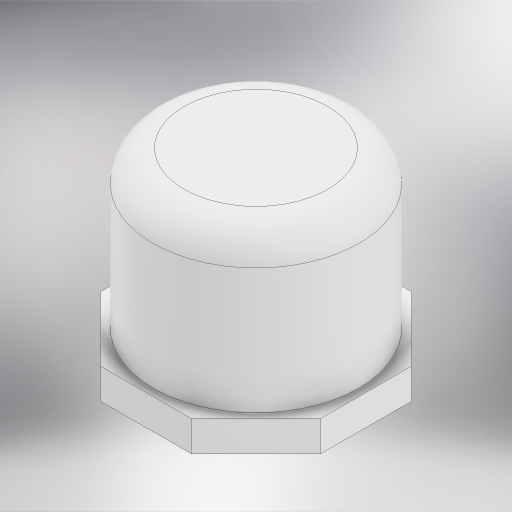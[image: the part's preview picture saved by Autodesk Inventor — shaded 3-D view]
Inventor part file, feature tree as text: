
AUTODESK INVENTOR PART (.ipt)
format: ipt  version: 2023 (Build 270158000, 158)  size: 310,272 bytes
history: native  units: mm
features: extrude x3, sketch x3, other x1, fillet x1
ambient origin geometry x8: Origin, YZ Plane, XZ Plane, XY Plane, X Axis, Y Axis, Z Axis, Center Point
bodies: Body1 (feature_tree)
feature tree (8):
  other  "Sólido1"
  extrude  "Extrusión1"  Depth=30.0mm TaperAngle=0.0deg
  extrude  "Extrusión2"  Depth=35.2mm
  fillet  "Empalme1"  Radius=35.2mm
  extrude  "Extrusión3"  Depth=35.2mm
  sketch  "Boceto1"  dims[d0=33.0mm d1=30.0mm d2=0.0mm]
  sketch  "Boceto2"  dims[d3=35.2mm d4=35.2mm d5=35.2mm]
  sketch  "Boceto3"  dims[d6=45.0deg d7=35.2mm d8=4.9mm d9=0.0mm d10=5.0mm d11=26.65mm d12=25.0mm d13=0.0mm]
